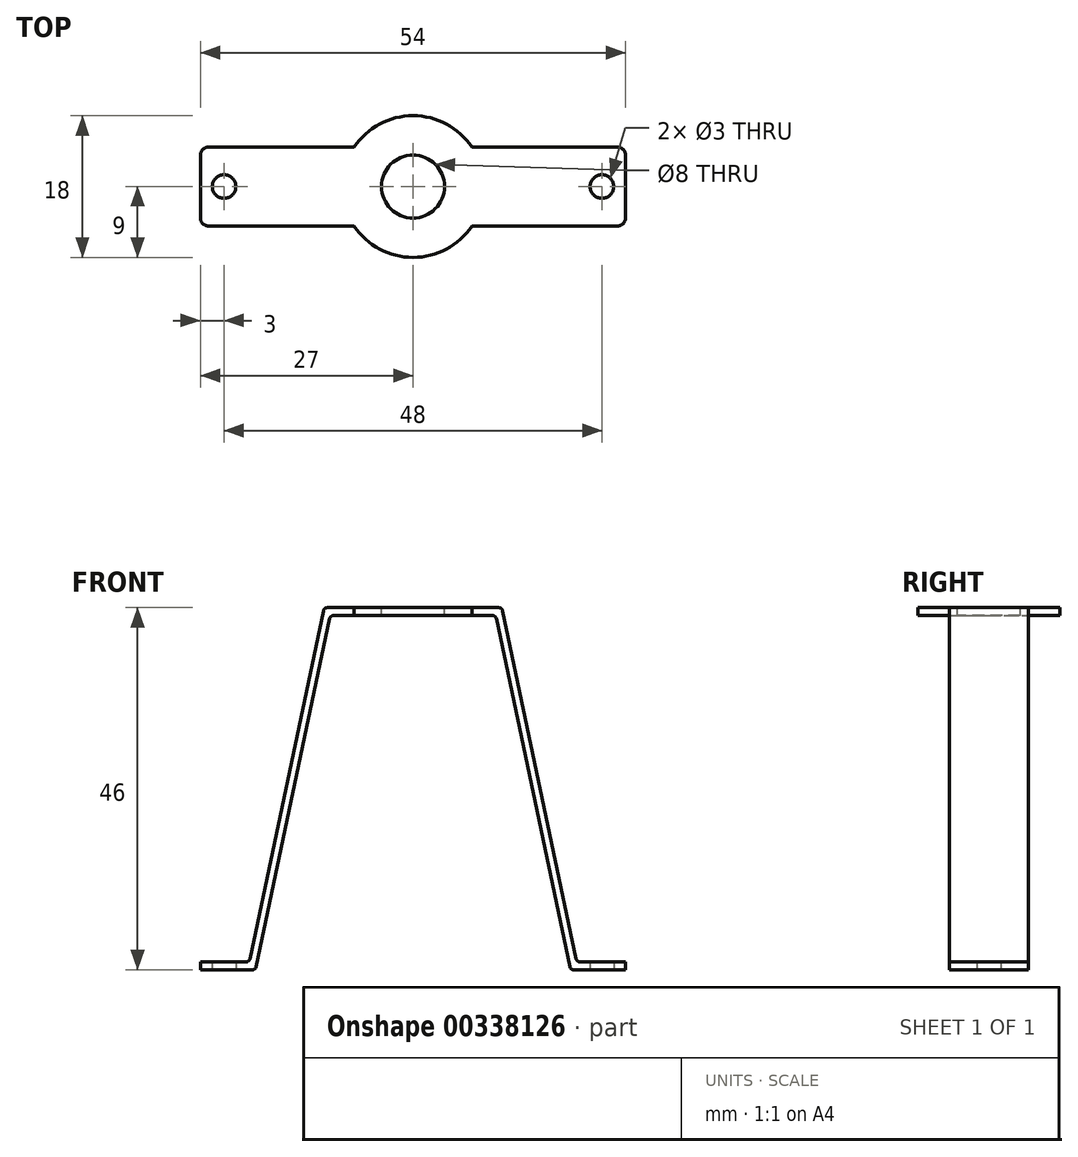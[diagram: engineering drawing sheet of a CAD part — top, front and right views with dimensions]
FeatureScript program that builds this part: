
annotation { "Feature Type Name" : "Feature", "Feature Type Description" : "" }
export const myFeature = defineFeature(function(context is Context, id is Id, definition is map)
    precondition{}
    {
        {
            var Q0;
            Q0=qCreatedBy(makeId("Front.planeOp"),FACE);
            var sketch = newSketch(context, id + "F0", { "sketchPlane" : qUnion([Q0])});
            skLineSegment(sketch, "E0", {"start": v(0, 50) * mm, "end": v(0, -50) * mm, "construction": true});
            skLineSegment(sketch, "E1", {"start": v(10.5, 45) * mm, "end": v(20, 0) * mm});
            skLineSegment(sketch, "E2", {"start": v(20, 0) * mm, "end": v(27, 0) * mm});
            skLineSegment(sketch, "E3.MirrorCS", {"start": v(-20, 0) * mm, "end": v(-27, 0) * mm});
            skLineSegment(sketch, "E4.MirrorCS", {"start": v(-10.5, 45) * mm, "end": v(-20, 0) * mm});
            skLineSegment(sketch, "E5", {"start": v(-10.5, 45) * mm, "end": v(10.5, 45) * mm});
            skLineSegment(sketch, "E6", {"start": v(-11.31, 46) * mm, "end": v(-20.81, 1) * mm});
            skLineSegment(sketch, "E7", {"start": v(-20.81, 1) * mm, "end": v(-27, 1) * mm});
            skLineSegment(sketch, "E8", {"start": v(-27, 1) * mm, "end": v(-27, 0) * mm});
            skLineSegment(sketch, "E9", {"start": v(-11.31, 46) * mm, "end": v(11.31, 46) * mm});
            skLineSegment(sketch, "E10", {"start": v(11.31, 46) * mm, "end": v(20.81, 1) * mm});
            skLineSegment(sketch, "E11", {"start": v(20.81, 1) * mm, "end": v(27, 1) * mm});
            skLineSegment(sketch, "E12", {"start": v(27, 1) * mm, "end": v(27, 0) * mm});
            skSolve(sketch);
        }
        {
            var Q0;
            Q0=qSketchRegion(id+"F0",true);
            extrude(context, id + "F1", {"entities" : qUnion([Q0]), "endBound" : BoundingType.SYMMETRIC, "depth" : 10 * mm});
        }
        {
            var Q0;
            Q0=makeQuery(id+"F1.opExtrude","SWEPT_EDGE",EDGE,{"disambiguationData":[OSD([sQuery(id+"F0.wireOp",EDGE,"E9"),sQuery(id+"F0.wireOp",EDGE,"E10")])]});
            var Q1;
            Q1=makeQuery(id+"F1.opExtrude","SWEPT_EDGE",EDGE,{"disambiguationData":[OSD([sQuery(id+"F0.wireOp",EDGE,"E6"),sQuery(id+"F0.wireOp",EDGE,"E9")])]});
            var Q2;
            Q2=makeQuery(id+"F1.opExtrude","SWEPT_EDGE",EDGE,{"disambiguationData":[OSD([sQuery(id+"F0.wireOp",EDGE,"E6"),sQuery(id+"F0.wireOp",EDGE,"E7")])]});
            var Q3;
            Q3=makeQuery(id+"F1.opExtrude","SWEPT_EDGE",EDGE,{"disambiguationData":[OSD([sQuery(id+"F0.wireOp",EDGE,"E10"),sQuery(id+"F0.wireOp",EDGE,"E11")])]});
            fillet(context, id + "F2", {"entities" : qUnion([Q0, Q1, Q2, Q3]), "radius" : 0.5 * mm, "tangentPropagation" : true, "allowEdgeOverflow" : false});
        }
        {
            var Q0;
            Q0=makeQuery(id+"F1.opExtrude","SWEPT_EDGE",EDGE,{"disambiguationData":[OSD([sQuery(id+"F0.wireOp",EDGE,"E4.MirrorCS"),sQuery(id+"F0.wireOp",EDGE,"E5")])]});
            var Q1;
            Q1=makeQuery(id+"F1.opExtrude","SWEPT_EDGE",EDGE,{"disambiguationData":[OSD([sQuery(id+"F0.wireOp",EDGE,"E1"),sQuery(id+"F0.wireOp",EDGE,"E5")])]});
            var Q2;
            Q2=makeQuery(id+"F1.opExtrude","SWEPT_EDGE",EDGE,{"disambiguationData":[OSD([sQuery(id+"F0.wireOp",EDGE,"E1"),sQuery(id+"F0.wireOp",EDGE,"E2")])]});
            var Q3;
            Q3=makeQuery(id+"F1.opExtrude","SWEPT_EDGE",EDGE,{"disambiguationData":[OSD([sQuery(id+"F0.wireOp",EDGE,"E3.MirrorCS"),sQuery(id+"F0.wireOp",EDGE,"E4.MirrorCS")])]});
            fillet(context, id + "F3", {"entities" : qUnion([Q0, Q1, Q2, Q3]), "radius" : 0.5 * mm, "tangentPropagation" : true, "allowEdgeOverflow" : false});
        }
        {
            var Q0;
            Q0=makeQuery(id+"F1.opExtrude","SWEPT_FACE",FACE,{"disambiguationData":[OSD([sQuery(id+"F0.wireOp",EDGE,"E9")])]});
            var sketch = newSketch(context, id + "F4", { "sketchPlane" : qUnion([Q0])});
            skCircle(sketch, "E13", {"center": v(0, 0) * mm, "radius": 9 * mm});
            skSolve(sketch);
        }
        {
            var Q0;
            Q0=qSketchRegion(id+"F4",true);
            var Q1;
            Q1=makeQuery(id+"F1.opExtrude","SWEPT_BODY",BODY,{"disambiguationData":[OSD([sQuery(id+"F0.wireOp",EDGE,"E1"),sQuery(id+"F0.wireOp",EDGE,"E2"),sQuery(id+"F0.wireOp",EDGE,"E3.MirrorCS"),sQuery(id+"F0.wireOp",EDGE,"E4.MirrorCS"),sQuery(id+"F0.wireOp",EDGE,"E5"),sQuery(id+"F0.wireOp",EDGE,"E6"),sQuery(id+"F0.wireOp",EDGE,"E7"),sQuery(id+"F0.wireOp",EDGE,"E8"),sQuery(id+"F0.wireOp",EDGE,"E9"),sQuery(id+"F0.wireOp",EDGE,"E10"),sQuery(id+"F0.wireOp",EDGE,"E11"),sQuery(id+"F0.wireOp",EDGE,"E12")])]});
            extrude(context, id + "F5", {"entities" : qUnion([Q0]), "operationType" : NewBodyOperationType.ADD, "oppositeDirection" : true, "endBoundEntityBody" : qUnion([Q1]), "depth" : 1 * mm});
        }
        {
            var Q0;
            Q0=makeQuery(id+"F5.boolean.opBoolean","MERGE",FACE,{"derivedFrom":[makeQuery(id+"F1.opExtrude","SWEPT_FACE",FACE,{"disambiguationData":[OSD([sQuery(id+"F0.wireOp",EDGE,"E9")])]}),makeQuery(id+"F5.opExtrude","CAP_FACE",FACE,{"disambiguationData":[OSD([sQuery(id+"F4.wireOp",EDGE,"E13")])],"isStart":true})]});
            var sketch = newSketch(context, id + "F6", { "sketchPlane" : qUnion([Q0])});
            skCircle(sketch, "E14", {"center": v(0, 0) * mm, "radius": 4 * mm});
            skSolve(sketch);
        }
        {
            var Q0;
            Q0=qSketchRegion(id+"F6",true);
            extrude(context, id + "F7", {"entities" : qUnion([Q0]), "operationType" : NewBodyOperationType.REMOVE, "endBound" : BoundingType.THROUGH_ALL, "oppositeDirection" : true, "depth" : 25 * mm});
        }
        {
            var Q0;
            Q0=qCreatedBy(makeId("Top.planeOp"),FACE);
            var sketch = newSketch(context, id + "F8", { "sketchPlane" : qUnion([Q0])});
            skLineSegment(sketch, "E15", {"start": v(-24, 0) * mm, "end": v(24, 0) * mm, "construction": true});
            skCircle(sketch, "E16", {"center": v(-24, 0) * mm, "radius": 1.5 * mm});
            skCircle(sketch, "E17", {"center": v(24, 0) * mm, "radius": 1.5 * mm});
            skSolve(sketch);
        }
        {
            var Q0;
            Q0=qSketchRegion(id+"F8",true);
            extrude(context, id + "F9", {"entities" : qUnion([Q0]), "operationType" : NewBodyOperationType.REMOVE, "endBound" : BoundingType.THROUGH_ALL, "depth" : 25 * mm});
        }
        {
            var Q0;
            Q0=makeQuery(id+"F1.opExtrude","CAP_EDGE",EDGE,{"disambiguationData":[OSD([sQuery(id+"F0.wireOp",EDGE,"E12")])],"isStart":false});
            var Q1;
            Q1=makeQuery(id+"F1.opExtrude","CAP_EDGE",EDGE,{"disambiguationData":[OSD([sQuery(id+"F0.wireOp",EDGE,"E12")])],"isStart":true});
            var Q2;
            Q2=makeQuery(id+"F1.opExtrude","CAP_EDGE",EDGE,{"disambiguationData":[OSD([sQuery(id+"F0.wireOp",EDGE,"E8")])],"isStart":false});
            var Q3;
            Q3=makeQuery(id+"F1.opExtrude","CAP_EDGE",EDGE,{"disambiguationData":[OSD([sQuery(id+"F0.wireOp",EDGE,"E8")])],"isStart":true});
            fillet(context, id + "F10", {"entities" : qUnion([Q0, Q1, Q2, Q3]), "radius" : 1 * mm, "tangentPropagation" : true, "allowEdgeOverflow" : false});
        }
    });
